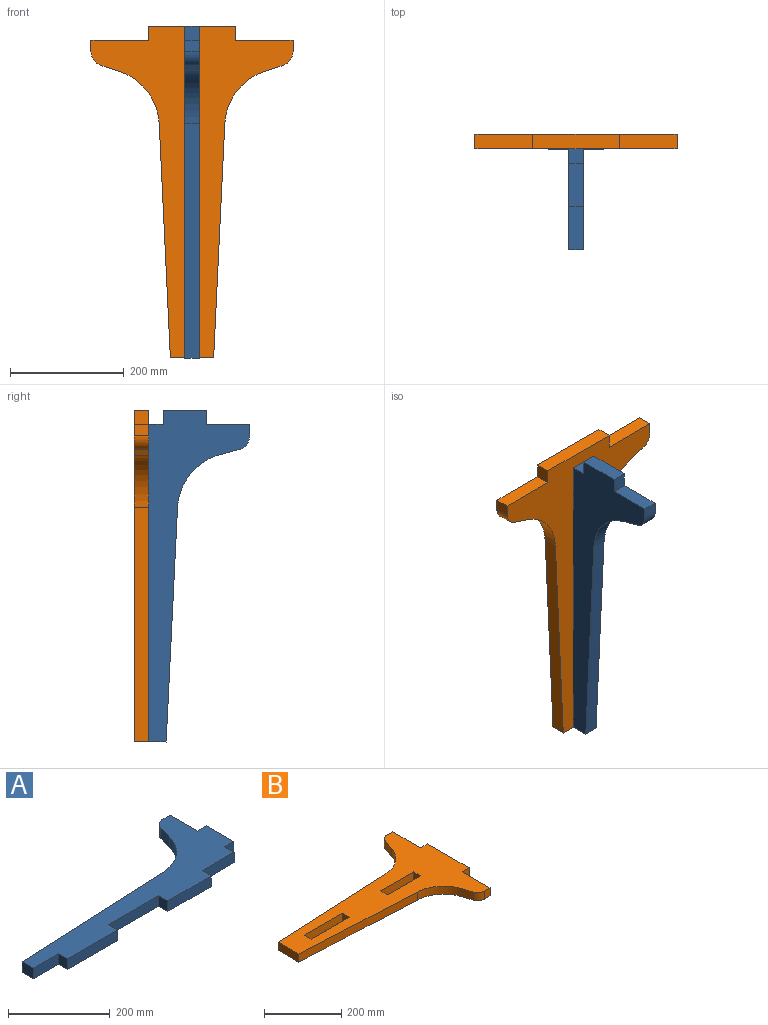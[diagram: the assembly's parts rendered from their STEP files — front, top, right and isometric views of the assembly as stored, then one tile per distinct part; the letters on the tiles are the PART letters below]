
ASSEMBLY  parts=2 mates=1
PART A: 22 faces, bbox 584.2x203.3x25.4 mm
  f0: plane 25.4x25.4mm, normal (0,-1,0), area 645.2mm2, adj f1,f19,f20,f21
  f1: plane 76.2x25.4mm, normal (1,0,0), area 1935.5mm2, adj f0,f2,f20,f21
  f2: plane 25.4x25.4mm, normal (0,1,0), area 645.2mm2, adj f1,f3,f20,f21
  f3: plane 76.2x25.4mm, normal (1,0,0), area 1935.5mm2, adj f2,f4,f20,f21
  f4: plane 25.4x19.67mm, normal (0,1,0), area 499.6mm2, adj f3,f5,f20,f21
  f5: cylinder r=25.4mm len=25.4mm, axis (0,0,-1), area 844.4mm2, adj f4,f6,f20,f21
  f6: plane 33.15x25.4mm, normal (-0.97,0.26,0), area 871.8mm2, adj f5,f7,f20,f21
  f7: cylinder r=101.6mm len=93.21mm, axis (0,0,-1), area 3252.6mm2, adj f6,f8,f20,f21
  f8: plane 412.54x25.4mm, normal (-0.05,1,0), area 10490.9mm2, adj f7,f9,f20,f21
  f9: plane 30.77x25.4mm, normal (-1,0,0), area 781.6mm2, adj f8,f10,f20,f21
  f10: plane 69.85x25.4mm, normal (0,-1,0), area 1774.2mm2, adj f9,f11,f20,f21
  f11: plane 25.51x25.4mm, normal (-1,0,0), area 647.8mm2, adj f10,f12,f20,f21
  f12: plane 139.7x25.4mm, normal (0,-1,0), area 3548.4mm2, adj f11,f13,f20,f21
  f13: plane 25.51x25.4mm, normal (1,0,0), area 647.8mm2, adj f12,f14,f20,f21
  f14: plane 139.7x25.4mm, normal (0,-1,0), area 3548.4mm2, adj f13,f15,f20,f21
  f15: plane 25.51x25.4mm, normal (-1,0,0), area 647.8mm2, adj f14,f16,f20,f21
  f16: plane 120.65x25.4mm, normal (0,-1,0), area 3064.5mm2, adj f15,f17,f20,f21
  f17: plane 25.51x25.4mm, normal (1,0,0), area 647.8mm2, adj f16,f18,f20,f21
  f18: plane 88.9x25.4mm, normal (0,-1,0), area 2258.1mm2, adj f17,f19,f20,f21
  f19: plane 25.4x25.4mm, normal (1,0,0), area 645.2mm2, adj f0,f18,f20,f21
  f20: plane 584.25x203.31mm, normal (0,0,1), area 40993.8mm2, adj f0,f1,f2,f3,f4,f5,f6,f7
  f21: plane 584.25x203.31mm, normal (0,0,-1), area 40993.8mm2, adj f0,f1,f2,f3,f4,f5,f6,f7
PART B: 26 faces, bbox 584.2x355.6x25.4 mm
  f0: plane 139.7x25.4mm, normal (0,-1,0), area 3548.4mm2, adj f1,f23,f24,f25
  f1: plane 25.4x25.4mm, normal (-1,0,0), area 645.2mm2, adj f0,f2,f24,f25
  f2: plane 139.7x25.4mm, normal (0,1,0), area 3548.4mm2, adj f1,f23,f24,f25
  f3: plane 120.65x25.4mm, normal (0,1,0), area 3064.5mm2, adj f4,f21,f24,f25
  f4: plane 25.4x25.4mm, normal (1,0,0), area 645.2mm2, adj f3,f5,f24,f25
  f5: plane 120.65x25.4mm, normal (0,-1,0), area 3064.5mm2, adj f4,f21,f24,f25
  f6: cylinder r=101.6mm len=91.78mm, axis (0,0,-1), area 3117.8mm2, adj f7,f22,f24,f25
  f7: plane 412.56x25.4mm, normal (-0.05,1,0), area 10490.9mm2, adj f6,f8,f24,f25
  f8: plane 76.2x25.4mm, normal (-1,0,0), area 1935.5mm2, adj f7,f9,f24,f25
  f9: plane 412.56x25.4mm, normal (-0.05,-1,0), area 10490.9mm2, adj f8,f10,f24,f25
  f10: cylinder r=101.6mm len=91.78mm, axis (0,0,-1), area 3117.8mm2, adj f9,f11,f24,f25
  f11: plane 32.63x25.4mm, normal (-0.95,-0.31,0), area 871.8mm2, adj f10,f12,f24,f25
  f12: cylinder r=25.4mm len=25.4mm, axis (0,0,-1), area 810mm2, adj f11,f13,f24,f25
  f13: plane 25.4x19.67mm, normal (0,-1,0), area 499.6mm2, adj f12,f14,f24,f25
  f14: plane 101.6x25.4mm, normal (1,0,0), area 2580.6mm2, adj f13,f15,f24,f25
  f15: plane 25.4x25.4mm, normal (0,-1,0), area 645.2mm2, adj f14,f16,f24,f25
  f16: plane 152.4x25.4mm, normal (1,0,0), area 3871mm2, adj f15,f17,f24,f25
  f17: plane 25.4x25.4mm, normal (0,1,0), area 645.2mm2, adj f16,f18,f24,f25
  f18: plane 101.6x25.4mm, normal (1,0,0), area 2580.6mm2, adj f17,f19,f24,f25
  f19: plane 25.4x19.67mm, normal (0,1,0), area 499.6mm2, adj f18,f20,f24,f25
  f20: cylinder r=25.4mm len=25.4mm, axis (0,0,-1), area 810mm2, adj f19,f22,f24,f25
  f21: plane 25.4x25.4mm, normal (-1,0,0), area 645.2mm2, adj f3,f5,f24,f25
  f22: plane 32.63x25.4mm, normal (-0.95,0.31,0), area 871.8mm2, adj f6,f20,f24,f25
  f23: plane 25.4x25.4mm, normal (1,0,0), area 645.2mm2, adj f0,f2,f24,f25
  f24: plane 584.2x355.6mm, normal (0,0,1), area 69373.2mm2, adj f0,f1,f2,f3,f4,f5,f6,f7
  f25: plane 584.2x355.6mm, normal (0,0,-1), area 69373.2mm2, adj f0,f1,f2,f3,f4,f5,f6,f7
PLACE A rot(axis=(0.71,0,0.71),180deg) t=(-139.95,887.46,-348.2)mm
PLACE B rot(axis=(0.58,-0.58,0.58),120deg) t=(320.51,439.59,-1003.2)mm
MATE fastened A.f18 <-> B.f24  axis (0,1,0) through (-127.25,414.19,-9.15)mm
